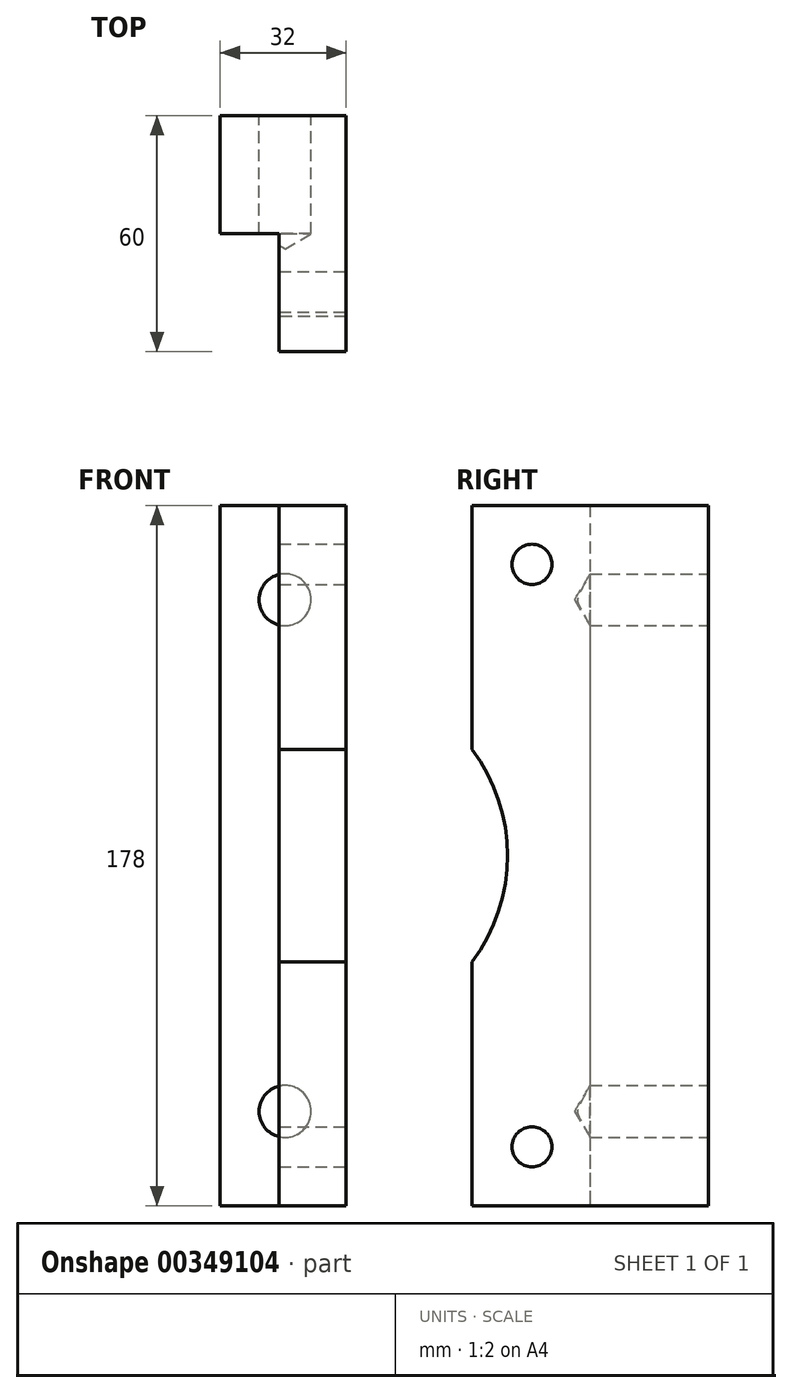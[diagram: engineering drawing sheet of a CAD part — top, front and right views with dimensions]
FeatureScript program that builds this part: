
annotation { "Feature Type Name" : "Feature", "Feature Type Description" : "" }
export const myFeature = defineFeature(function(context is Context, id is Id, definition is map)
    precondition{}
    {
        {
            var Q0;
            Q0=qCreatedBy(makeId("Right.planeOp"),FACE);
            var sketch = newSketch(context, id + "F0", { "sketchPlane" : qUnion([Q0])});
            skCircle(sketch, "E0", {"center": v(0, 0) * mm, "radius": 28.5 * mm});
            skLineSegment(sketch, "E1", {"start": v(51.22, 74) * mm, "end": v(51.22, -74) * mm});
            skLineSegment(sketch, "E2", {"start": v(0, 0) * mm, "end": v(51.22, 74) * mm});
            skLineSegment(sketch, "E3", {"start": v(51.22, -74) * mm, "end": v(0, 0) * mm});
            skCircle(sketch, "E4", {"center": v(0, 0) * mm, "radius": 41 * mm});
            skCircle(sketch, "E5", {"center": v(0, 0) * mm, "radius": 45 * mm});
            skCircle(sketch, "E6", {"center": v(0, 0) * mm, "radius": 104 * mm});
            skLineSegment(sketch, "E7", {"start": v(96, 40) * mm, "end": v(96, -40) * mm});
            skLineSegment(sketch, "E8", {"start": v(66.22, 100.25) * mm, "end": v(66.22, -99.44) * mm});
            skSolve(sketch);
        }
        {
            var Q0;
            Q0=qCreatedBy(makeId("Right.planeOp"),FACE);
            cPlane(context, id + "F1", {"entities" : qUnion([Q0]), "cplaneType" : CPlaneType.OFFSET, "offset" : 48 * mm, "oppositeDirection" : true, "width" : 150 * mm, "height" : 150 * mm});
        }
        {
            var Q0;
            Q0=qCreatedBy(makeId("Right.planeOp"),FACE);
            cPlane(context, id + "F2", {"entities" : qUnion([Q0]), "cplaneType" : CPlaneType.OFFSET, "offset" : 9.5 * mm, "oppositeDirection" : true, "width" : 150 * mm, "height" : 150 * mm});
        }
        {
            var Q0;
            Q0=qCreatedBy(id+"F2.planeOp",FACE);
            var sketch = newSketch(context, id + "F3", { "sketchPlane" : qUnion([Q0])});
            skCircle(sketch, "E9", {"center": v(0, 0) * mm, "radius": 144 * mm});
            skSolve(sketch);
        }
        {
            var Q0;
            Q0=qCreatedBy(id+"F1.planeOp",FACE);
            var sketch = newSketch(context, id + "F4", { "sketchPlane" : qUnion([Q0])});
            skCircle(sketch, "E10", {"center": v(51.22, 74) * mm, "radius": 5 * mm});
            skCircle(sketch, "E11", {"center": v(51.22, -74) * mm, "radius": 5 * mm});
            skArc(sketch, "E12", {"start": v(36, 27) * mm, "mid": v(45, 0) * mm, "end": v(36, -27) * mm});
            skLineSegment(sketch, "E13", {"start": v(36, 27) * mm, "end": v(36, 89) * mm});
            skLineSegment(sketch, "E14", {"start": v(36, 89) * mm, "end": v(96, 89) * mm});
            skLineSegment(sketch, "E15", {"start": v(96, 89) * mm, "end": v(96, -89) * mm});
            skLineSegment(sketch, "E16", {"start": v(96, -89) * mm, "end": v(36, -89) * mm});
            skLineSegment(sketch, "E17", {"start": v(36, -89) * mm, "end": v(36, -27) * mm});
            skSolve(sketch);
        }
        {
            var Q0;
            Q0 = qSketchRegion(id + "F4", true);
            var Q1;
            Q1=makeQuery(id+"F4.imprint","IMPRINT",FACE,{"disambiguationData":[TD([[makeQuery(id+"F4.imprint","IMPRINT",EDGE,{"derivedFrom":sQuery(id+"F4.wireOp",EDGE,"E10")}),1.0]])]});
            var Q2;
            Q2=makeQuery(id+"F4.imprint","IMPRINT",FACE,{"disambiguationData":[TD([[makeQuery(id+"F4.imprint","IMPRINT",EDGE,{"derivedFrom":sQuery(id+"F4.wireOp",EDGE,"E11")}),1.0]])]});
            extrude(context, id + "F5", {"entities" : qUnion([Q0, Q1, Q2]), "depth" : 17 * mm});
        }
        {
            var Q0;
            Q0=makeQuery(id+"F5.opExtrude","SWEPT_FACE",FACE,{"disambiguationData":[OSD([sQuery(id+"F4.wireOp",EDGE,"E15")])]});
            var sketch = newSketch(context, id + "F6", { "sketchPlane" : qUnion([Q0])});
            skCircle(sketch, "E18", {"center": v(46.5, 65) * mm, "radius": 6 * mm});
            skCircle(sketch, "E19", {"center": v(46.5, -65) * mm, "radius": 6 * mm});
            skSolve(sketch);
        }
        {
            var Q0;
            Q0=makeQuery(id+"F5.opExtrude","CAP_FACE",FACE,{"disambiguationData":[OSD([sQuery(id+"F4.wireOp",EDGE,"E10"),sQuery(id+"F4.wireOp",EDGE,"E11"),sQuery(id+"F4.wireOp",EDGE,"E12"),sQuery(id+"F4.wireOp",EDGE,"E13"),sQuery(id+"F4.wireOp",EDGE,"E14"),sQuery(id+"F4.wireOp",EDGE,"E15"),sQuery(id+"F4.wireOp",EDGE,"E16"),sQuery(id+"F4.wireOp",EDGE,"E17")])],"isStart":true});
            var sketch = newSketch(context, id + "F7", { "sketchPlane" : qUnion([Q0])});
            skLineSegment(sketch, "E20.bottom", {"start": v(-96, 89) * mm, "end": v(-66, 89) * mm});
            skLineSegment(sketch, "E20.top", {"start": v(-96, -89) * mm, "end": v(-66, -89) * mm});
            skLineSegment(sketch, "E20.left", {"start": v(-96, 89) * mm, "end": v(-96, -89) * mm});
            skLineSegment(sketch, "E20.right", {"start": v(-66, 89) * mm, "end": v(-66, -89) * mm});
            skSolve(sketch);
        }
        {
            var Q0;
            Q0 = qSketchRegion(id + "F7", true);
            extrude(context, id + "F8", {"entities" : qUnion([Q0]), "operationType" : NewBodyOperationType.ADD, "depth" : 15 * mm});
        }
        {
            var Q0;
            Q0=makeQuery(id+"F8.opExtrude","CAP_FACE",FACE,{"disambiguationData":[OSD([sQuery(id+"F7.wireOp",EDGE,"E20.bottom"),sQuery(id+"F7.wireOp",EDGE,"E20.top"),sQuery(id+"F7.wireOp",EDGE,"E20.left"),sQuery(id+"F7.wireOp",EDGE,"E20.right")])],"isStart":false});
            var sketch = newSketch(context, id + "F9", { "sketchPlane" : qUnion([Q0])});
            skLineSegment(sketch, "E21.bottom", {"start": v(-96, 89) * mm, "end": v(-36, 89) * mm});
            skLineSegment(sketch, "E21.top", {"start": v(-96, -89) * mm, "end": v(-36, -89) * mm});
            skLineSegment(sketch, "E21.left", {"start": v(-96, 89) * mm, "end": v(-96, -89) * mm});
            skLineSegment(sketch, "E21.right", {"start": v(-36, 89) * mm, "end": v(-36, 27) * mm});
            skArc(sketch, "E22", {"start": v(-36, -27) * mm, "mid": v(-45, 0) * mm, "end": v(-36, 27) * mm});
            skLineSegment(sketch, "E23.trimOffspring", {"start": v(-36, -27) * mm, "end": v(-36, -89) * mm});
            skSolve(sketch);
        }
        {
            var Q0;
            Q0=sQuery(id+"F0.wireOp",VERTEX,"E1.start");
            var Q1;
            Q1=sQuery(id+"F0.wireOp",VERTEX,"E3.start");
            var Q2;
            Q2=makeQuery(id+"F5.opExtrude","SWEPT_BODY",BODY,{"disambiguationData":[OSD([sQuery(id+"F4.wireOp",EDGE,"E12"),sQuery(id+"F4.wireOp",EDGE,"E13"),sQuery(id+"F4.wireOp",EDGE,"E14"),sQuery(id+"F4.wireOp",EDGE,"E15"),sQuery(id+"F4.wireOp",EDGE,"E16"),sQuery(id+"F4.wireOp",EDGE,"E17")])]});
            hole(context, id + "F10", {"style" : HoleStyle.SIMPLE, "endStyle" : HoleEndStyle.BLIND, "holeDiameter" : 10.2 * mm, "holeDepth" : 80 * mm, "isTappedThrough" : true, "tappedDepth" : 12 * mm, "tapClearance" : 3, "locations" : qUnion([Q0, Q1]), "scope" : qUnion([Q2])});
        }
        {
            var Q0;
            Q0=sQuery(id+"F6.wireOp",VERTEX,"E18.center");
            var Q1;
            Q1=sQuery(id+"F6.wireOp",VERTEX,"E19.center");
            var Q2;
            Q2=makeQuery(id+"F5.opExtrude","SWEPT_BODY",BODY,{"disambiguationData":[OSD([sQuery(id+"F4.wireOp",EDGE,"E12"),sQuery(id+"F4.wireOp",EDGE,"E13"),sQuery(id+"F4.wireOp",EDGE,"E14"),sQuery(id+"F4.wireOp",EDGE,"E15"),sQuery(id+"F4.wireOp",EDGE,"E16"),sQuery(id+"F4.wireOp",EDGE,"E17")])]});
            hole(context, id + "F11", {"style" : HoleStyle.SIMPLE, "endStyle" : HoleEndStyle.BLIND, "standardTappedOrClearance" : lookupTablePath({ "standard" : "ISO", "fit" : "Normal", "size" : "M12", "type" : "Clearance" }), "standardBlindInLast" : lookupTablePath({ "fit" : "Standard", "standard" : "ISO", "size" : "M12", "type" : "Clearance" }), "holeDiameter" : 13.2 * mm, "holeDepth" : 30 * mm, "isTappedThrough" : true, "tappedDepth" : 12 * mm, "tapClearance" : 3, "locations" : qUnion([Q0, Q1]), "scope" : qUnion([Q2])});
        }
    });
